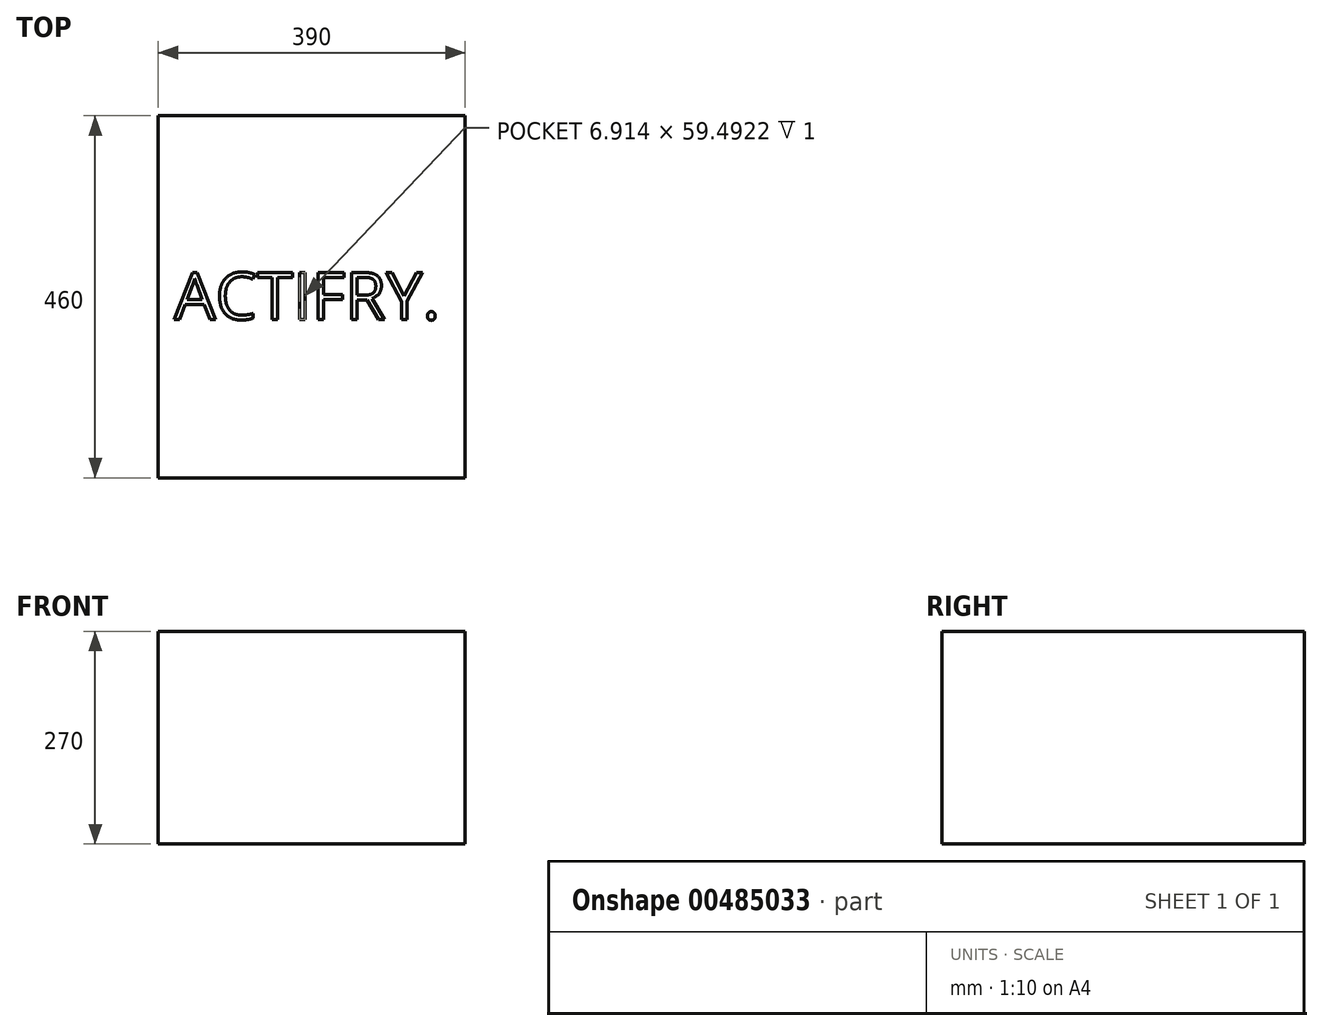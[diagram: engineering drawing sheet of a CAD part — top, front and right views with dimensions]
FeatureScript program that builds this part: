
annotation { "Feature Type Name" : "Feature", "Feature Type Description" : "" }
export const myFeature = defineFeature(function(context is Context, id is Id, definition is map)
    precondition{}
    {
        {
            var Q0;
            Q0=qCreatedBy(makeId("Top.planeOp"),FACE);
            var sketch = newSketch(context, id + "F0", { "sketchPlane" : qUnion([Q0])});
            skLineSegment(sketch, "E0.bottom", {"start": v(195, -230) * mm, "end": v(-195, -230) * mm});
            skLineSegment(sketch, "E0.top", {"start": v(195, 230) * mm, "end": v(-195, 230) * mm});
            skLineSegment(sketch, "E0.left", {"start": v(195, -230) * mm, "end": v(195, 230) * mm});
            skLineSegment(sketch, "E0.right", {"start": v(-195, -230) * mm, "end": v(-195, 230) * mm});
            skPoint(sketch, "E0.middle", {"position": v(0, 0) * mm});
            skSolve(sketch);
        }
        {
            var Q0;
            Q0=makeQuery(id+"F0.imprint","IMPRINT",FACE,{"disambiguationData":[TD([[makeQuery(id+"F0.imprint","IMPRINT",EDGE,{"derivedFrom":sQuery(id+"F0.wireOp",EDGE,"E0.bottom")}),-1.0]])]});
            extrude(context, id + "F1", {"entities" : qUnion([Q0]), "depth" : 270 * mm});
        }
        {
            var Q0;
            Q0=makeQuery(id+"F1.opExtrude","CAP_FACE",FACE,{"disambiguationData":[OSD([sQuery(id+"F0.wireOp",EDGE,"E0.bottom"),sQuery(id+"F0.wireOp",EDGE,"E0.top"),sQuery(id+"F0.wireOp",EDGE,"E0.left"),sQuery(id+"F0.wireOp",EDGE,"E0.right")])],"isStart":false});
            var sketch = newSketch(context, id + "F2", { "sketchPlane" : qUnion([Q0])});
            skText(sketch, "E1", { "text": "ACTIFRY.", "fontName": "OpenSans-Regular.ttf"});
            const initialGuessF2  = {"E1": [-0.175, -0.02874, 1, 0, 0.06]};
            skSetInitialGuess(sketch, initialGuessF2);
            skSolve(sketch);
        }
        {
            var Q0;
            Q0 = qSketchRegion(id + "F2", true);
            extrude(context, id + "F3", {"entities" : qUnion([Q0]), "operationType" : NewBodyOperationType.REMOVE, "oppositeDirection" : true, "depth" : 1 * mm});
        }
    });
